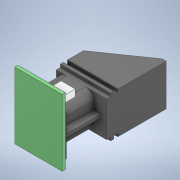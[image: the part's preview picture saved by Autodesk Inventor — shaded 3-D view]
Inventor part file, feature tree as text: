
AUTODESK INVENTOR PART (.ipt)
format: ipt  version: 2020 (Build 240168000, 168)  size: 171,008 bytes
history: native  units: mm
features: sketch x1, other x1
ambient origin geometry x8: Origin, YZ Plane, XZ Plane, XY Plane, X Axis, Y Axis, Z Axis, Center Point
bodies: Solid1 (feature_tree)
feature tree (2):
  sketch  "Sketch1"
  other  "Cut-Extrude3"
